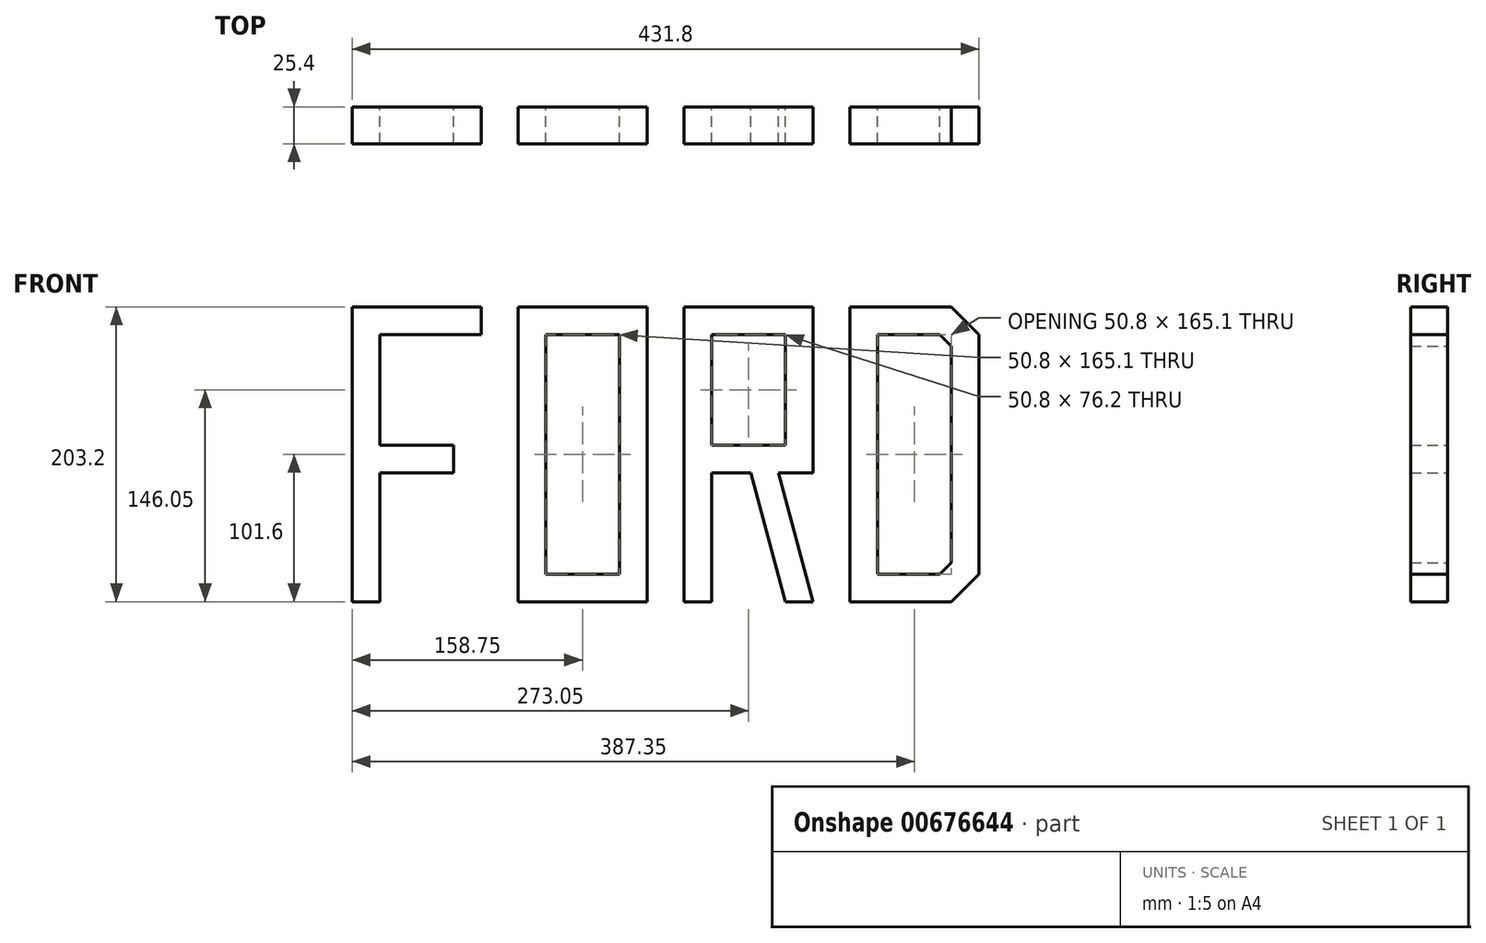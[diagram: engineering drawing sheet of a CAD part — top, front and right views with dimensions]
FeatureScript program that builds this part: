
annotation { "Feature Type Name" : "Feature", "Feature Type Description" : "" }
export const myFeature = defineFeature(function(context is Context, id is Id, definition is map)
    precondition{}
    {
        {
            var Q0;
            Q0=qCreatedBy(makeId("Front.planeOp"),FACE);
            var sketch = newSketch(context, id + "F0", { "sketchPlane" : qUnion([Q0])});
            skLineSegment(sketch, "E0", {"start": v(0, 0) * mm, "end": v(0, -203.2) * mm});
            skLineSegment(sketch, "E1", {"start": v(0, -203.2) * mm, "end": v(19.05, -203.2) * mm});
            skLineSegment(sketch, "E2", {"start": v(19.05, -203.2) * mm, "end": v(19.05, -114.3) * mm});
            skLineSegment(sketch, "E3", {"start": v(19.05, -114.3) * mm, "end": v(69.85, -114.3) * mm});
            skLineSegment(sketch, "E4", {"start": v(69.85, -114.3) * mm, "end": v(69.85, -95.25) * mm});
            skLineSegment(sketch, "E5", {"start": v(69.85, -95.25) * mm, "end": v(19.05, -95.25) * mm});
            skLineSegment(sketch, "E6", {"start": v(19.05, -95.25) * mm, "end": v(19.05, -19.05) * mm});
            skLineSegment(sketch, "E7", {"start": v(19.05, -19.05) * mm, "end": v(88.9, -19.05) * mm});
            skLineSegment(sketch, "E8", {"start": v(88.9, -19.05) * mm, "end": v(88.9, 0) * mm});
            skLineSegment(sketch, "E9", {"start": v(88.9, 0) * mm, "end": v(0, 0) * mm});
            skLineSegment(sketch, "E10", {"start": v(114.3, 0) * mm, "end": v(114.3, -203.2) * mm});
            skLineSegment(sketch, "E11", {"start": v(114.3, -203.2) * mm, "end": v(203.2, -203.2) * mm});
            skLineSegment(sketch, "E12", {"start": v(203.2, -203.2) * mm, "end": v(203.2, 0) * mm});
            skLineSegment(sketch, "E13", {"start": v(203.2, 0) * mm, "end": v(114.3, 0) * mm});
            skLineSegment(sketch, "E14", {"start": v(133.35, -184.15) * mm, "end": v(184.15, -184.15) * mm});
            skLineSegment(sketch, "E15", {"start": v(184.15, -184.15) * mm, "end": v(184.15, -19.05) * mm});
            skLineSegment(sketch, "E16", {"start": v(184.15, -19.05) * mm, "end": v(133.35, -19.05) * mm});
            skLineSegment(sketch, "E17", {"start": v(133.35, -19.05) * mm, "end": v(133.35, -184.15) * mm});
            skLineSegment(sketch, "E18", {"start": v(228.6, 0) * mm, "end": v(228.6, -203.2) * mm});
            skLineSegment(sketch, "E19", {"start": v(228.6, -203.2) * mm, "end": v(247.65, -203.2) * mm});
            skLineSegment(sketch, "E20", {"start": v(247.65, -203.2) * mm, "end": v(247.65, -114.3) * mm});
            skLineSegment(sketch, "E21", {"start": v(247.65, -114.3) * mm, "end": v(274.63, -114.3) * mm});
            skLineSegment(sketch, "E22", {"start": v(274.63, -114.3) * mm, "end": v(298.45, -203.2) * mm});
            skLineSegment(sketch, "E23", {"start": v(298.45, -203.2) * mm, "end": v(317.5, -203.2) * mm});
            skLineSegment(sketch, "E24", {"start": v(317.5, -203.2) * mm, "end": v(293.68, -114.3) * mm});
            skLineSegment(sketch, "E25", {"start": v(293.68, -114.3) * mm, "end": v(317.5, -114.3) * mm});
            skLineSegment(sketch, "E26", {"start": v(317.5, -114.3) * mm, "end": v(317.5, 0) * mm});
            skLineSegment(sketch, "E27", {"start": v(317.5, 0) * mm, "end": v(228.6, 0) * mm});
            skLineSegment(sketch, "E28", {"start": v(247.65, -19.05) * mm, "end": v(247.65, -95.25) * mm});
            skLineSegment(sketch, "E29", {"start": v(247.65, -95.25) * mm, "end": v(298.45, -95.25) * mm});
            skLineSegment(sketch, "E30", {"start": v(298.45, -95.25) * mm, "end": v(298.45, -19.05) * mm});
            skLineSegment(sketch, "E31", {"start": v(298.45, -19.05) * mm, "end": v(247.65, -19.05) * mm});
            skLineSegment(sketch, "E32", {"start": v(342.9, 0) * mm, "end": v(342.9, -203.2) * mm});
            skLineSegment(sketch, "E33", {"start": v(342.9, -203.2) * mm, "end": v(412.75, -203.2) * mm});
            skLineSegment(sketch, "E34", {"start": v(412.75, -203.2) * mm, "end": v(431.8, -184.15) * mm});
            skLineSegment(sketch, "E35", {"start": v(431.8, -184.15) * mm, "end": v(431.8, -19.05) * mm});
            skLineSegment(sketch, "E36", {"start": v(431.8, -19.05) * mm, "end": v(412.75, 0) * mm});
            skLineSegment(sketch, "E37", {"start": v(412.75, 0) * mm, "end": v(342.9, 0) * mm});
            skLineSegment(sketch, "E38", {"start": v(361.95, -184.15) * mm, "end": v(404.86, -184.15) * mm});
            skLineSegment(sketch, "E39", {"start": v(404.86, -184.15) * mm, "end": v(412.75, -176.26) * mm});
            skLineSegment(sketch, "E40", {"start": v(412.75, -176.26) * mm, "end": v(412.75, -26.94) * mm});
            skLineSegment(sketch, "E41", {"start": v(412.75, -26.94) * mm, "end": v(404.86, -19.05) * mm});
            skLineSegment(sketch, "E42", {"start": v(404.86, -19.05) * mm, "end": v(361.95, -19.05) * mm});
            skLineSegment(sketch, "E43", {"start": v(361.95, -184.15) * mm, "end": v(361.95, -19.05) * mm});
            skLineSegment(sketch, "E44", {"start": v(133.35, -184.15) * mm, "end": v(133.35, -203.2) * mm, "construction": true});
            skLineSegment(sketch, "E45", {"start": v(133.35, -184.15) * mm, "end": v(114.3, -184.15) * mm, "construction": true});
            skLineSegment(sketch, "E46", {"start": v(19.05, -114.3) * mm, "end": v(19.05, -95.25) * mm, "construction": true});
            skLineSegment(sketch, "E47", {"start": v(298.45, -19.05) * mm, "end": v(298.45, 0) * mm, "construction": true});
            skLineSegment(sketch, "E48", {"start": v(317.5, -19.05) * mm, "end": v(298.45, -19.05) * mm, "construction": true});
            skLineSegment(sketch, "E49", {"start": v(361.95, -19.05) * mm, "end": v(342.9, -19.05) * mm, "construction": true});
            skLineSegment(sketch, "E50", {"start": v(361.95, 0) * mm, "end": v(361.95, -19.05) * mm, "construction": true});
            skLineSegment(sketch, "E51", {"start": v(408.8, -180.2) * mm, "end": v(422.28, -193.67) * mm, "construction": true});
            skLineSegment(sketch, "E52", {"start": v(412.75, -26.94) * mm, "end": v(431.8, -26.94) * mm, "construction": true});
            skLineSegment(sketch, "E53", {"start": v(317.5, 0) * mm, "end": v(342.9, 0) * mm, "construction": true});
            skLineSegment(sketch, "E54", {"start": v(203.2, 0) * mm, "end": v(228.6, 0) * mm, "construction": true});
            skLineSegment(sketch, "E55", {"start": v(184.15, -184.15) * mm, "end": v(203.2, -184.15) * mm, "construction": true});
            skLineSegment(sketch, "E56", {"start": v(184.15, -19.05) * mm, "end": v(184.15, 0) * mm, "construction": true});
            skLineSegment(sketch, "E57", {"start": v(228.6, -95.25) * mm, "end": v(247.65, -95.25) * mm, "construction": true});
            skLineSegment(sketch, "E58", {"start": v(88.9, -19.05) * mm, "end": v(114.3, -19.05) * mm, "construction": true});
            skLineSegment(sketch, "E59", {"start": v(408.8, -23) * mm, "end": v(422.28, -9.53) * mm, "construction": true});
            skSolve(sketch);
        }
        {
            var Q0;
            Q0=makeQuery(id+"F0.imprint","IMPRINT",FACE,{"disambiguationData":[TD([[makeQuery(id+"F0.imprint","IMPRINT",EDGE,{"derivedFrom":sQuery(id+"F0.wireOp",EDGE,"E0")}),1.0]])]});
            var Q1;
            Q1=makeQuery(id+"F0.imprint","IMPRINT",FACE,{"disambiguationData":[TD([[makeQuery(id+"F0.imprint","IMPRINT",EDGE,{"derivedFrom":sQuery(id+"F0.wireOp",EDGE,"E10")}),1.0]])]});
            var Q2;
            Q2=makeQuery(id+"F0.imprint","IMPRINT",FACE,{"disambiguationData":[TD([[makeQuery(id+"F0.imprint","IMPRINT",EDGE,{"derivedFrom":sQuery(id+"F0.wireOp",EDGE,"E18")}),1.0]])]});
            var Q3;
            Q3=makeQuery(id+"F0.imprint","IMPRINT",FACE,{"disambiguationData":[TD([[makeQuery(id+"F0.imprint","IMPRINT",EDGE,{"derivedFrom":sQuery(id+"F0.wireOp",EDGE,"E32")}),1.0]])]});
            extrude(context, id + "F1", {"entities" : qUnion([Q0, Q1, Q2, Q3]), "depth" : 25.4 * mm, "offsetDistance" : 25.4 * mm});
        }
    });
